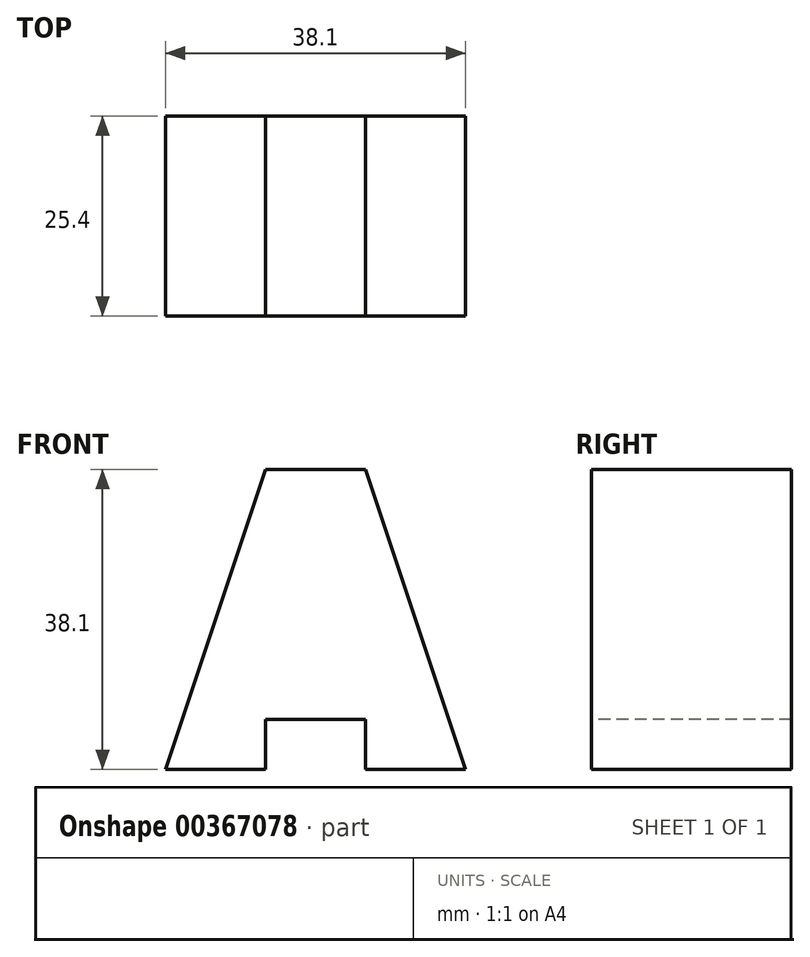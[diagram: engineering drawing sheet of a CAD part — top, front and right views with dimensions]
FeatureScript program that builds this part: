
annotation { "Feature Type Name" : "Feature", "Feature Type Description" : "" }
export const myFeature = defineFeature(function(context is Context, id is Id, definition is map)
    precondition{}
    {
        {
            var Q0;
            Q0=qCreatedBy(makeId("Right.planeOp"),FACE);
            var sketch = newSketch(context, id + "F0", { "sketchPlane" : qUnion([Q0])});
            skLineSegment(sketch, "E0", {"start": v(0, 0) * mm, "end": v(0, 38.1) * mm});
            skLineSegment(sketch, "E1", {"start": v(0, 38.1) * mm, "end": v(25.4, 38.1) * mm});
            skLineSegment(sketch, "E2", {"start": v(25.4, 38.1) * mm, "end": v(25.4, 0) * mm});
            skLineSegment(sketch, "E3", {"start": v(25.4, 0) * mm, "end": v(0, 0) * mm});
            skSolve(sketch);
        }
        {
            var Q0;
            Q0=makeQuery(id+"F0.imprint","IMPRINT",FACE,{"disambiguationData":[TD([[makeQuery(id+"F0.imprint","IMPRINT",EDGE,{"derivedFrom":sQuery(id+"F0.wireOp",EDGE,"E0")}),-1.0]])]});
            extrude(context, id + "F1", {"entities" : qUnion([Q0]), "depth" : 38.1 * mm});
        }
        {
            var Q0;
            Q0=qCreatedBy(makeId("Front.planeOp"),FACE);
            var sketch = newSketch(context, id + "F2", { "sketchPlane" : qUnion([Q0])});
            skLineSegment(sketch, "E4", {"start": v(12.7, 0) * mm, "end": v(12.7, 6.35) * mm});
            skLineSegment(sketch, "E5", {"start": v(12.7, 6.35) * mm, "end": v(25.4, 6.35) * mm});
            skLineSegment(sketch, "E6", {"start": v(25.4, 6.35) * mm, "end": v(25.4, 0) * mm});
            skLineSegment(sketch, "E7", {"start": v(25.4, 0) * mm, "end": v(12.7, 0) * mm});
            skSolve(sketch);
        }
        {
            var Q0;
            Q0 = qSketchRegion(id + "F2", true);
            extrude(context, id + "F3", {"entities" : qUnion([Q0]), "operationType" : NewBodyOperationType.REMOVE, "oppositeDirection" : true, "depth" : 25.4 * mm});
        }
        {
            var Q0;
            Q0=makeQuery(id+"F1.opExtrude","SWEPT_FACE",FACE,{"disambiguationData":[OSD([sQuery(id+"F0.wireOp",EDGE,"E0")])]});
            var sketch = newSketch(context, id + "F4", { "sketchPlane" : qUnion([Q0])});
            skLineSegment(sketch, "E8", {"start": v(25.4, 38.1) * mm, "end": v(38.1, 0) * mm});
            skLineSegment(sketch, "E9", {"start": v(38.1, 0) * mm, "end": v(38.1, 38.1) * mm});
            skLineSegment(sketch, "E10", {"start": v(38.1, 38.1) * mm, "end": v(25.4, 38.1) * mm});
            skSolve(sketch);
        }
        {
            var Q0;
            Q0 = qSketchRegion(id + "F4", true);
            extrude(context, id + "F5", {"entities" : qUnion([Q0]), "operationType" : NewBodyOperationType.REMOVE, "oppositeDirection" : true, "depth" : 25.4 * mm});
        }
        {
            var Q0;
            Q0=qCreatedBy(makeId("Front.planeOp"),FACE);
            var sketch = newSketch(context, id + "F6", { "sketchPlane" : qUnion([Q0])});
            skLineSegment(sketch, "E11", {"start": v(0, 0) * mm, "end": v(12.7, 38.1) * mm});
            skLineSegment(sketch, "E12", {"start": v(12.7, 38.1) * mm, "end": v(0, 38.1) * mm});
            skLineSegment(sketch, "E13", {"start": v(0, 38.1) * mm, "end": v(0, 0) * mm});
            skSolve(sketch);
        }
        {
            var Q0;
            Q0=makeQuery(id+"F6.imprint","IMPRINT",FACE,{"disambiguationData":[TD([[makeQuery(id+"F6.imprint","IMPRINT",EDGE,{"derivedFrom":sQuery(id+"F6.wireOp",EDGE,"E11")}),1.0]])]});
            extrude(context, id + "F7", {"entities" : qUnion([Q0]), "operationType" : NewBodyOperationType.REMOVE, "oppositeDirection" : true, "depth" : 25.4 * mm});
        }
    });
